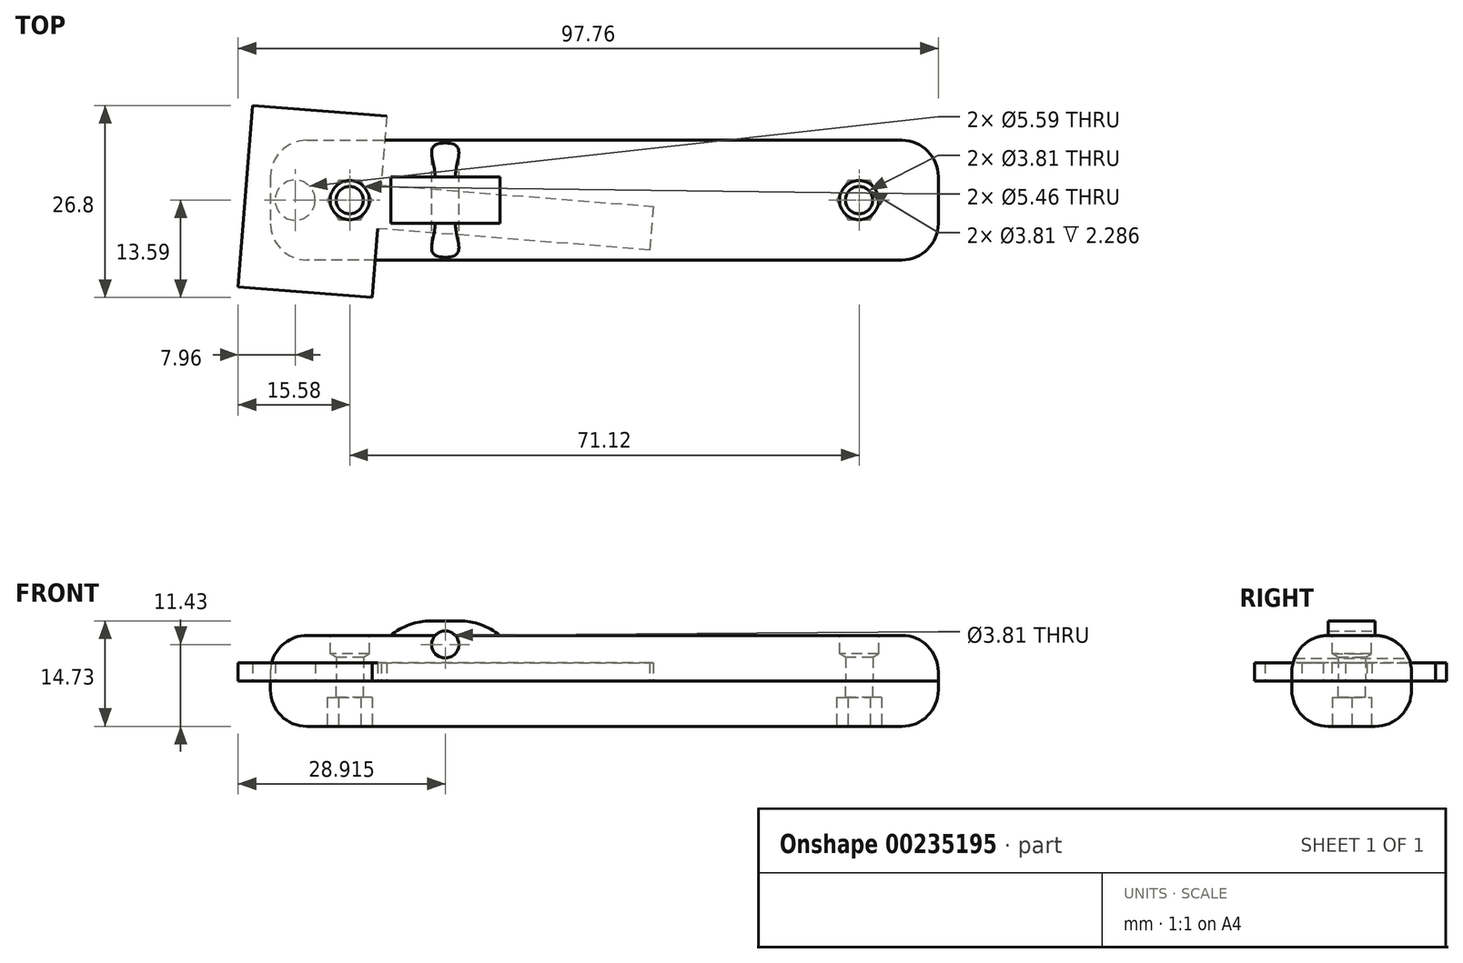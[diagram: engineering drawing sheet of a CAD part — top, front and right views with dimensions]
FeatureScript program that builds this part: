
annotation { "Feature Type Name" : "Feature", "Feature Type Description" : "" }
export const myFeature = defineFeature(function(context is Context, id is Id, definition is map)
    precondition{}
    {
        {
            var Q0;
            Q0=qCreatedBy(makeId("Top.planeOp"),FACE);
            var sketch = newSketch(context, id + "F0", { "sketchPlane" : qUnion([Q0])});
            skLineSegment(sketch, "E0", {"start": v(-49.15, 13.2) * mm, "end": v(-30.4, 11.73) * mm});
            skLineSegment(sketch, "E1", {"start": v(-30.4, 11.73) * mm, "end": v(-31.17, 2.11) * mm});
            skLineSegment(sketch, "E2", {"start": v(-31.17, 2.11) * mm, "end": v(6.82, -0.88) * mm});
            skLineSegment(sketch, "E3", {"start": v(6.82, -0.88) * mm, "end": v(6.34, -6.96) * mm});
            skLineSegment(sketch, "E4", {"start": v(6.34, -6.96) * mm, "end": v(-31.65, -3.97) * mm});
            skLineSegment(sketch, "E5", {"start": v(-31.65, -3.97) * mm, "end": v(-32.4, -13.59) * mm});
            skLineSegment(sketch, "E6", {"start": v(-32.4, -13.59) * mm, "end": v(-51.14, -12.11) * mm});
            skLineSegment(sketch, "E7", {"start": v(-51.14, -12.11) * mm, "end": v(-49.15, 13.2) * mm});
            skLineSegment(sketch, "E8", {"start": v(-50.07, 1.15) * mm, "end": v(-50.07, 1.15) * mm});
            skLineSegment(sketch, "E9", {"start": v(-50.14, 0.55) * mm, "end": v(-43.18, 0) * mm});
            skCircle(sketch, "E10", {"center": v(-43.18, 0) * mm, "radius": 2.8 * mm});
            skPoint(sketch, "E11", {"position": v(-50.14, 0.55) * mm});
            skSolve(sketch);
        }
        {
            var Q0;
            Q0=makeQuery(id+"F0.imprint","IMPRINT",FACE,{"disambiguationData":[TD([[makeQuery(id+"F0.imprint","IMPRINT",EDGE,{"derivedFrom":sQuery(id+"F0.wireOp",EDGE,"E0")}),-1.0]])]});
            extrude(context, id + "F1", {"entities" : qUnion([Q0]), "depth" : 2.54 * mm});
        }
        {
            var Q0;
            Q0=qCreatedBy(makeId("Top.planeOp"),FACE);
            var sketch = newSketch(context, id + "F2", { "sketchPlane" : qUnion([Q0])});
            skPoint(sketch, "E12.rect.middle", {"position": v(0, 0) * mm});
            skCircle(sketch, "E13", {"center": v(-35.56, 0) * mm, "radius": 1.9 * mm});
            skLineSegment(sketch, "E14", {"start": v(-35.56, 0) * mm, "end": v(-46.62, 0) * mm});
            skLineSegment(sketch, "E15", {"start": v(0, 8.36) * mm, "end": v(-46.62, 8.36) * mm});
            skLineSegment(sketch, "E16", {"start": v(-46.62, 8.36) * mm, "end": v(-46.62, 0) * mm});
            skLineSegment(sketch, "E17.MirrorCS", {"start": v(0, -8.36) * mm, "end": v(-46.62, -8.36) * mm});
            skLineSegment(sketch, "E18.MirrorCS", {"start": v(-46.62, -8.36) * mm, "end": v(-46.62, 0) * mm});
            skLineSegment(sketch, "E19.MirrorCS", {"start": v(35.56, 0) * mm, "end": v(46.62, 0) * mm});
            skCircle(sketch, "E20.MirrorC", {"center": v(35.56, 0) * mm, "radius": 1.9 * mm});
            skLineSegment(sketch, "E21.MirrorCS", {"start": v(0, 8.36) * mm, "end": v(46.62, 8.36) * mm});
            skLineSegment(sketch, "E22.MirrorCS", {"start": v(46.62, 8.36) * mm, "end": v(46.62, 0) * mm});
            skLineSegment(sketch, "E23.MirrorCS", {"start": v(46.62, -8.36) * mm, "end": v(46.62, 0) * mm});
            skLineSegment(sketch, "E24.MirrorCS", {"start": v(0, -8.36) * mm, "end": v(46.62, -8.36) * mm});
            skSolve(sketch);
        }
        {
            var Q0;
            Q0=makeQuery(id+"F2.imprint","IMPRINT",FACE,{"disambiguationData":[TD([[makeQuery(id+"F2.imprint","IMPRINT",EDGE,{"derivedFrom":sQuery(id+"F2.wireOp",EDGE,"E13")}),-1.0]])]});
            extrude(context, id + "F3", {"entities" : qUnion([Q0]), "depth" : 6.35 * mm, "offsetDistance" : 25.4 * mm});
        }
        {
            var Q0;
            Q0=qSketchRegion(id+"F2",true);
            extrude(context, id + "F4", {"entities" : qUnion([Q0]), "oppositeDirection" : true, "depth" : 6.35 * mm, "offsetDistance" : 25.4 * mm});
        }
        {
            var Q0;
            Q0=makeQuery(id+"F3.opExtrude","CAP_EDGE",EDGE,{"disambiguationData":[OSD([sQuery(id+"F2.wireOp",EDGE,"E17.MirrorCS"),sQuery(id+"F2.wireOp",EDGE,"E24.MirrorCS")])],"isStart":false});
            var Q1;
            Q1=makeQuery(id+"F3.opExtrude","CAP_EDGE",EDGE,{"disambiguationData":[OSD([sQuery(id+"F2.wireOp",EDGE,"E16"),sQuery(id+"F2.wireOp",EDGE,"E18.MirrorCS")])],"isStart":false});
            var Q2;
            Q2=makeQuery(id+"F3.opExtrude","CAP_EDGE",EDGE,{"disambiguationData":[OSD([sQuery(id+"F2.wireOp",EDGE,"E15"),sQuery(id+"F2.wireOp",EDGE,"E21.MirrorCS")])],"isStart":false});
            var Q3;
            Q3=makeQuery(id+"F3.opExtrude","CAP_EDGE",EDGE,{"disambiguationData":[OSD([sQuery(id+"F2.wireOp",EDGE,"E22.MirrorCS"),sQuery(id+"F2.wireOp",EDGE,"E23.MirrorCS")])],"isStart":false});
            var Q4;
            Q4=makeQuery(id+"F3.opExtrude","SWEPT_EDGE",EDGE,{"disambiguationData":[OSD([sQuery(id+"F2.wireOp",EDGE,"E17.MirrorCS"),sQuery(id+"F2.wireOp",EDGE,"E18.MirrorCS")])]});
            var Q5;
            Q5=makeQuery(id+"F3.opExtrude","SWEPT_EDGE",EDGE,{"disambiguationData":[OSD([sQuery(id+"F2.wireOp",EDGE,"E15"),sQuery(id+"F2.wireOp",EDGE,"E16")])]});
            var Q6;
            Q6=makeQuery(id+"F3.opExtrude","SWEPT_EDGE",EDGE,{"disambiguationData":[OSD([sQuery(id+"F2.wireOp",EDGE,"E23.MirrorCS"),sQuery(id+"F2.wireOp",EDGE,"E24.MirrorCS")])]});
            var Q7;
            Q7=makeQuery(id+"F3.opExtrude","SWEPT_EDGE",EDGE,{"disambiguationData":[OSD([sQuery(id+"F2.wireOp",EDGE,"E21.MirrorCS"),sQuery(id+"F2.wireOp",EDGE,"E22.MirrorCS")])]});
            fillet(context, id + "F5", {"entities" : qUnion([Q0, Q1, Q2, Q3, Q4, Q5, Q6, Q7]), "radius" : 5.08 * mm, "tangentPropagation" : true, "allowEdgeOverflow" : false});
        }
        {
            var Q0;
            Q0=makeQuery(id+"F4.opExtrude","CAP_EDGE",EDGE,{"disambiguationData":[OSD([sQuery(id+"F2.wireOp",EDGE,"E16"),sQuery(id+"F2.wireOp",EDGE,"E18.MirrorCS")])],"isStart":false});
            var Q1;
            Q1=makeQuery(id+"F4.opExtrude","CAP_EDGE",EDGE,{"disambiguationData":[OSD([sQuery(id+"F2.wireOp",EDGE,"E17.MirrorCS"),sQuery(id+"F2.wireOp",EDGE,"E24.MirrorCS")])],"isStart":false});
            var Q2;
            Q2=makeQuery(id+"F4.opExtrude","CAP_EDGE",EDGE,{"disambiguationData":[OSD([sQuery(id+"F2.wireOp",EDGE,"E22.MirrorCS"),sQuery(id+"F2.wireOp",EDGE,"E23.MirrorCS")])],"isStart":false});
            var Q3;
            Q3=makeQuery(id+"F4.opExtrude","CAP_EDGE",EDGE,{"disambiguationData":[OSD([sQuery(id+"F2.wireOp",EDGE,"E15"),sQuery(id+"F2.wireOp",EDGE,"E21.MirrorCS")])],"isStart":false});
            var Q4;
            Q4=makeQuery(id+"F4.opExtrude","SWEPT_EDGE",EDGE,{"disambiguationData":[OSD([sQuery(id+"F2.wireOp",EDGE,"E23.MirrorCS"),sQuery(id+"F2.wireOp",EDGE,"E24.MirrorCS")])]});
            var Q5;
            Q5=makeQuery(id+"F4.opExtrude","SWEPT_EDGE",EDGE,{"disambiguationData":[OSD([sQuery(id+"F2.wireOp",EDGE,"E21.MirrorCS"),sQuery(id+"F2.wireOp",EDGE,"E22.MirrorCS")])]});
            var Q6;
            Q6=makeQuery(id+"F4.opExtrude","SWEPT_EDGE",EDGE,{"disambiguationData":[OSD([sQuery(id+"F2.wireOp",EDGE,"E17.MirrorCS"),sQuery(id+"F2.wireOp",EDGE,"E18.MirrorCS")])]});
            var Q7;
            Q7=makeQuery(id+"F4.opExtrude","SWEPT_EDGE",EDGE,{"disambiguationData":[OSD([sQuery(id+"F2.wireOp",EDGE,"E15"),sQuery(id+"F2.wireOp",EDGE,"E16")])]});
            fillet(context, id + "F6", {"entities" : qUnion([Q0, Q1, Q2, Q3, Q4, Q5, Q6, Q7]), "radius" : 5.08 * mm, "tangentPropagation" : true, "allowEdgeOverflow" : false});
        }
        {
            var Q0;
            Q0=makeQuery(id+"F3.opExtrude","CAP_FACE",FACE,{"disambiguationData":[OSD([sQuery(id+"F2.wireOp",EDGE,"E13"),sQuery(id+"F2.wireOp",EDGE,"E15"),sQuery(id+"F2.wireOp",EDGE,"E16"),sQuery(id+"F2.wireOp",EDGE,"E17.MirrorCS"),sQuery(id+"F2.wireOp",EDGE,"E18.MirrorCS"),sQuery(id+"F2.wireOp",EDGE,"E20.MirrorC"),sQuery(id+"F2.wireOp",EDGE,"E21.MirrorCS"),sQuery(id+"F2.wireOp",EDGE,"E22.MirrorCS"),sQuery(id+"F2.wireOp",EDGE,"E23.MirrorCS"),sQuery(id+"F2.wireOp",EDGE,"E24.MirrorCS")])],"isStart":false});
            var sketch = newSketch(context, id + "F7", { "sketchPlane" : qUnion([Q0])});
            skLineSegment(sketch, "E25.rect.bottom", {"start": v(-14.6, -3.27) * mm, "end": v(-29.85, -3.27) * mm});
            skLineSegment(sketch, "E25.rect.top", {"start": v(-14.6, 3.27) * mm, "end": v(-29.85, 3.27) * mm});
            skLineSegment(sketch, "E25.rect.left", {"start": v(-14.6, -3.27) * mm, "end": v(-14.6, 3.27) * mm});
            skLineSegment(sketch, "E25.rect.right", {"start": v(-29.85, -3.27) * mm, "end": v(-29.85, 3.27) * mm});
            skPoint(sketch, "E25.rect.middle", {"position": v(-22.23, 0) * mm});
            skSolve(sketch);
        }
        {
            var Q0;
            Q0=makeQuery(id+"F7.imprint","IMPRINT",FACE,{"disambiguationData":[TD([[makeQuery(id+"F7.imprint","IMPRINT",EDGE,{"derivedFrom":sQuery(id+"F7.wireOp",EDGE,"E25.rect.bottom")}),-1.0]])]});
            extrude(context, id + "F8", {"entities" : qUnion([Q0]), "operationType" : NewBodyOperationType.ADD, "depth" : 2.03 * mm});
        }
        {
            var Q0;
            Q0=makeQuery(id+"F8.opExtrude","CAP_EDGE",EDGE,{"disambiguationData":[OSD([sQuery(id+"F7.wireOp",EDGE,"E25.rect.right")])],"isStart":false});
            var Q1;
            Q1=makeQuery(id+"F8.opExtrude","CAP_EDGE",EDGE,{"disambiguationData":[OSD([sQuery(id+"F7.wireOp",EDGE,"E25.rect.left")])],"isStart":false});
            fillet(context, id + "F9", {"entities" : qUnion([Q0, Q1]), "radius" : 8.9 * mm, "tangentPropagation" : true, "allowEdgeOverflow" : false});
        }
        {
            var Q0;
            Q0=makeQuery(id+"F8.opExtrude","SWEPT_FACE",FACE,{"disambiguationData":[OSD([sQuery(id+"F7.wireOp",EDGE,"E25.rect.bottom")])]});
            var sketch = newSketch(context, id + "F10", { "sketchPlane" : qUnion([Q0])});
            skPoint(sketch, "E26", {"position": v(-22.23, 6.35) * mm});
            skPoint(sketch, "E27", {"position": v(-22.23, 5.08) * mm});
            skSolve(sketch);
        }
        {
            var Q0;
            Q0=sQuery(id+"F10.wireOp",VERTEX,"E27");
            var Q1;
            Q1=makeQuery(id+"F3.opExtrude","SWEPT_BODY",BODY,{"disambiguationData":[OSD([sQuery(id+"F2.wireOp",EDGE,"E12.rect.bottom"),sQuery(id+"F2.wireOp",EDGE,"E12.rect.top"),sQuery(id+"F2.wireOp",EDGE,"E12.rect.left"),sQuery(id+"F2.wireOp",EDGE,"E12.rect.right"),sQuery(id+"F2.wireOp",EDGE,"E13"),sQuery(id+"F2.wireOp",EDGE,"5560e56f-8cb0-4288-8763-c49c99b43e4f")])]});
            hole(context, id + "F11", {"style" : HoleStyle.SIMPLE, "holeDiameter" : 3.8 * mm, "endStyle" : HoleEndStyle.THROUGH, "oppositeDirection" : true, "locations" : qUnion([Q0]), "scope" : qUnion([Q1]), "tappedDepth" : 12.7 * mm, "tapClearance" : 3});
        }
        {
            var Q0;
            Q0=sQuery(id+"F10.wireOp",VERTEX,"E27");
            var Q1;
            Q1=makeQuery(id+"F3.opExtrude","SWEPT_BODY",BODY,{"disambiguationData":[OSD([sQuery(id+"F2.wireOp",EDGE,"E12.rect.bottom"),sQuery(id+"F2.wireOp",EDGE,"E12.rect.top"),sQuery(id+"F2.wireOp",EDGE,"E12.rect.left"),sQuery(id+"F2.wireOp",EDGE,"E12.rect.right"),sQuery(id+"F2.wireOp",EDGE,"E13"),sQuery(id+"F2.wireOp",EDGE,"5560e56f-8cb0-4288-8763-c49c99b43e4f")])]});
            hole(context, id + "F12", {"style" : HoleStyle.SIMPLE, "holeDiameter" : 3.8 * mm, "endStyle" : HoleEndStyle.THROUGH, "locations" : qUnion([Q0]), "scope" : qUnion([Q1]), "tappedDepth" : 12.7 * mm, "tapClearance" : 3});
        }
        {
            var Q0;
            Q0=makeQuery(id+"F7.imprint","IMPRINT",FACE,{"disambiguationData":[TD([[makeQuery(id+"F7.imprint","IMPRINT",EDGE,{"derivedFrom":sQuery(id+"F7.wireOp",EDGE,"E25.rect.bottom")}),1.0]])]});
            var sketch = newSketch(context, id + "F13", { "sketchPlane" : qUnion([Q0])});
            skPoint(sketch, "E28", {"position": v(35.56, 0) * mm});
            skPoint(sketch, "E29", {"position": v(-35.56, 0) * mm});
            skSolve(sketch);
        }
        {
            var Q0;
            Q0=sQuery(id+"F13.wireOp",VERTEX,"E28");
            var Q1;
            Q1=sQuery(id+"F13.wireOp",VERTEX,"E29");
            var Q2;
            Q2=makeQuery(id+"F3.opExtrude","SWEPT_BODY",BODY,{"disambiguationData":[OSD([sQuery(id+"F2.wireOp",EDGE,"E13"),sQuery(id+"F2.wireOp",EDGE,"E15"),sQuery(id+"F2.wireOp",EDGE,"E16"),sQuery(id+"F2.wireOp",EDGE,"E17.MirrorCS"),sQuery(id+"F2.wireOp",EDGE,"E18.MirrorCS"),sQuery(id+"F2.wireOp",EDGE,"E20.MirrorC"),sQuery(id+"F2.wireOp",EDGE,"E21.MirrorCS"),sQuery(id+"F2.wireOp",EDGE,"E22.MirrorCS"),sQuery(id+"F2.wireOp",EDGE,"E23.MirrorCS"),sQuery(id+"F2.wireOp",EDGE,"E24.MirrorCS")])]});
            hole(context, id + "F14", {"style" : HoleStyle.SIMPLE, "endStyle" : HoleEndStyle.BLIND, "holeDiameter" : 5.46 * mm, "holeDepth" : 2.54 * mm, "isTappedThrough" : true, "tappedDepth" : 12.7 * mm, "tapClearance" : 3, "locations" : qUnion([Q0, Q1]), "scope" : qUnion([Q2])});
        }
        {
            var Q0;
            Q0=makeQuery(id+"F4.opExtrude","CAP_FACE",FACE,{"disambiguationData":[OSD([sQuery(id+"F2.wireOp",EDGE,"E13"),sQuery(id+"F2.wireOp",EDGE,"E15"),sQuery(id+"F2.wireOp",EDGE,"E16"),sQuery(id+"F2.wireOp",EDGE,"E17.MirrorCS"),sQuery(id+"F2.wireOp",EDGE,"E18.MirrorCS"),sQuery(id+"F2.wireOp",EDGE,"E20.MirrorC"),sQuery(id+"F2.wireOp",EDGE,"E21.MirrorCS"),sQuery(id+"F2.wireOp",EDGE,"E22.MirrorCS"),sQuery(id+"F2.wireOp",EDGE,"E23.MirrorCS"),sQuery(id+"F2.wireOp",EDGE,"E24.MirrorCS")])],"isStart":false});
            var sketch = newSketch(context, id + "F15", { "sketchPlane" : qUnion([Q0])});
            skPoint(sketch, "E30", {"position": v(-35.56, 0) * mm});
            skPoint(sketch, "E31", {"position": v(35.56, 0) * mm});
            skCircle(sketch, "E32.cCircle", {"center": v(-35.56, 0) * mm, "radius": 2.73 * mm, "construction": true});
            skLineSegment(sketch, "E32.0", {"start": v(-32.4, 0) * mm, "end": v(-33.98, -2.73) * mm});
            skLineSegment(sketch, "E32.1", {"start": v(-33.98, -2.73) * mm, "end": v(-37.14, -2.73) * mm});
            skLineSegment(sketch, "E32.2", {"start": v(-37.14, -2.73) * mm, "end": v(-38.71, 0) * mm});
            skLineSegment(sketch, "E32.3", {"start": v(-38.71, 0) * mm, "end": v(-37.14, 2.73) * mm});
            skLineSegment(sketch, "E32.4", {"start": v(-37.14, 2.73) * mm, "end": v(-33.98, 2.73) * mm});
            skLineSegment(sketch, "E32.5", {"start": v(-33.98, 2.73) * mm, "end": v(-32.4, 0) * mm});
            skPoint(sketch, "E32.0.midPoint", {"position": v(-33.2, -1.37) * mm});
            skCircle(sketch, "E33.cCircle", {"center": v(35.56, 0) * mm, "radius": 2.73 * mm, "construction": true});
            skLineSegment(sketch, "E33.0", {"start": v(38.71, 0) * mm, "end": v(37.14, -2.73) * mm});
            skLineSegment(sketch, "E33.1", {"start": v(37.14, -2.73) * mm, "end": v(33.98, -2.73) * mm});
            skLineSegment(sketch, "E33.2", {"start": v(33.98, -2.73) * mm, "end": v(32.4, 0) * mm});
            skLineSegment(sketch, "E33.3", {"start": v(32.4, 0) * mm, "end": v(33.98, 2.73) * mm});
            skLineSegment(sketch, "E33.4", {"start": v(33.98, 2.73) * mm, "end": v(37.14, 2.73) * mm});
            skLineSegment(sketch, "E33.5", {"start": v(37.14, 2.73) * mm, "end": v(38.71, 0) * mm});
            skPoint(sketch, "E33.0.midPoint", {"position": v(37.92, -1.37) * mm});
            skSolve(sketch);
        }
        {
            var Q0;
            Q0=makeQuery(id+"F15.imprint","IMPRINT",FACE,{"disambiguationData":[TD([[makeQuery(id+"F15.imprint","IMPRINT",EDGE,{"derivedFrom":sQuery(id+"F15.wireOp",EDGE,"E32.0")}),-1.0]])]});
            var Q1;
            Q1=makeQuery(id+"F15.imprint","IMPRINT",FACE,{"disambiguationData":[TD([[makeQuery(id+"F15.imprint","IMPRINT",EDGE,{"derivedFrom":sQuery(id+"F15.wireOp",EDGE,"E33.0")}),-1.0]])]});
            extrude(context, id + "F16", {"entities" : qUnion([Q0, Q1]), "operationType" : NewBodyOperationType.REMOVE, "oppositeDirection" : true, "depth" : 4.06 * mm});
        }
        {
            var Q0;
            Q0=makeQuery(id+"F1.opExtrude","SWEPT_BODY",BODY,{"disambiguationData":[OSD([sQuery(id+"F0.wireOp",EDGE,"E0"),sQuery(id+"F0.wireOp",EDGE,"E1"),sQuery(id+"F0.wireOp",EDGE,"E2"),sQuery(id+"F0.wireOp",EDGE,"E3"),sQuery(id+"F0.wireOp",EDGE,"E4"),sQuery(id+"F0.wireOp",EDGE,"E5"),sQuery(id+"F0.wireOp",EDGE,"E6"),sQuery(id+"F0.wireOp",EDGE,"E7"),sQuery(id+"F0.wireOp",EDGE,"00a381d7-7105-4c5e-a130-2b6659f4c8b5")])]});
            transform(context, id + "F17", {"entities" : qUnion([Q0]), "transformType" : TransformType.TRANSLATION_3D, "dx" : 0 * mm, "dy" : 0 * mm, "dz" : 0 * mm, "makeCopy" : true});
        }
    });
